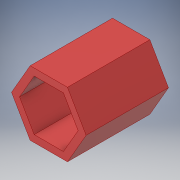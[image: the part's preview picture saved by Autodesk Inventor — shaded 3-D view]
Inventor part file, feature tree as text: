
AUTODESK INVENTOR PART (.ipt)
format: ipt  version: 2019.4 (Build 234330000, 330)  size: 103,424 bytes
history: native  units: in
note: dims shown in document units (in); Inventor stores cm internally (conversion verified against a paired STEP export)
features: extrude x1, sketch x1
ambient origin geometry x8: Origin, YZ Plane, XZ Plane, XY Plane, X Axis, Y Axis, Z Axis, Center Point
bodies: Solid1 (feature_tree)
feature tree (2):
  extrude  "Extrusion1"  Depth=0.385in
  sketch  "Sketch1"  dims[d0=0.49in d1=0.385in d2=0.625in d3=0.0in]
